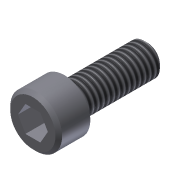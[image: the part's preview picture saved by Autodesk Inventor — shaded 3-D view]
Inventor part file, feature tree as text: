
AUTODESK INVENTOR PART (.ipt)
format: ipt  version: 2013 (Build 170138000, 138)  size: 110,080 bytes
history: native  units: in
note: dims shown in document units (in); Inventor stores cm internally (conversion verified against a paired STEP export)
features: extrude x3, sketch x3, chamfer x2, thread x1
ambient origin geometry x8: Origin, YZ Plane, XZ Plane, XY Plane, X Axis, Y Axis, Z Axis, Center Point
bodies: Solid1 (feature_tree)
feature tree (9):
  extrude  "Extrusion1"  Depth=0.19in TaperAngle=0.0deg
  extrude  "Extrusion2"  Depth=0.5in TaperAngle=0.0deg
  extrude  "Extrusion3"  Depth=0.125in TaperAngle=0.0deg
  thread  "Thread1"  [1 undecoded]
  chamfer  "Chamfer1"  Distance=0.02in Angle=45.0deg
  chamfer  "Chamfer2"  Distance=0.02in Angle=45.0deg
  sketch  "Sketch1"  dims[d0=0.312in d1=0.19in d2=0.0in]
  sketch  "Sketch2"  dims[d3=0.19in d4=0.5in d5=0.0in]
  sketch  "Sketch3"  dims[d6=0.1562in d7=0.125in d8=0.0in d9=1.0in d10=0.0in d11=0.02in d12=0.125in d13=45.0deg d14=0.02in d15=0.125in d16=45.0deg]
note: 1 required parameter value undecoded (feature->parameter linkage not recoverable at this tier; creation-order binding heuristic only, values carry confidence <= 0.55)
